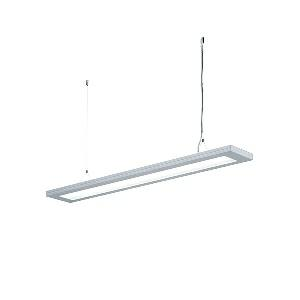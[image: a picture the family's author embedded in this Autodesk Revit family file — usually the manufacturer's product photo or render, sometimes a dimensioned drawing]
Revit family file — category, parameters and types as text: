
# Revit family: lavigo_-_dpp_16000_840_r_g2_00801373_008e
name_source: partatom
category: Lighting Fixtures
units: mm (PartAtom-declared; Revit-internal decimal feet)

## family parameters
Cut with Voids When Loaded = No
Host = Face
Light Source = No
Part Type = Normal
Room Calculation Point = No
Round Connector Dimension = Use Diameter
Shared = No

## types (1)
- LAVIGO - DPP 16000/840/R/G2 (1 x LED, 16450 lm, 4000K)
    Apparent Load = 112 VA
    Approval mark = CE
    CIE Flux Codes = 60 87 97 11 100
    Color Rendering = 80-89
    Color Temperature = 4000K
    Control Gear = Electronic ballast
    Default Elevation = 1800 mm
    Description = DPP 16000/840/R/G2|Suspended luminaire|light source: LED|connected load: 220-240 V, 50/60 Hz|Power consumption: approx. 112 W|standby: approx. 0,50|luminous flux: 16450 lm|luminous efficacy: 146 lm/W|light distribution: Direct/indirect|direct ratio: approx. 11 %|colour temperature: Cold white, ca. 4000 K|color rendering index (CRI): >= 80|chromaticity tolerance:  3 SDCM|System of protection: IP 20|technology: Presence and daylight sensor control (PIR)|luminaire body|material: Steel/plastic|surface: Powder coatet|colour: Silver metallic|lamp cover: Polycarbonate (PC), Clear|mains lead: 1.00 m With free stranded wires|Fastening: Steel cable 0.3 - 0.7 m|decorative contrast side parts: Flint grey|glare control: Prism aperture|luminance(L65): <= 2800 cd/m|unified glare rating(4H 8H): <=  16|special features: Canopy colour (pure white), Push button in luminaire head, Direct light component with edge light and light-guide technology for homogenous light exit, Flicker-free, Integrated light and presence sensor PIR, Retrofittable with TALK module, Separated, direct and indirect light individually adjustable|
    Frequency = 50 Hz
    Height = 36 mm
    Lamp = 1 x LED
    Lamp Light Flux = 16450 lm
    Lamp count = 1
    Length = 1245 mm
    Luminous efficacy = 147 lm/W
    Manufacturer = Waldmann
    ModVariant = No
    Model = 00801373
    Mounting Place = Ceiling
    Mounting Type = Pendant
    Number of Poles = 1
    OnlyDefault = Yes
    Power Factor = 1
    Product Name = LAVIGO - DPP 16000/840/R/G2
    Product group = Suspended luminaire
    ProductGroupID = 9
    Protection Class = Protection class I
    Protection Degree = IP 20
    RLX_Detail_Level = 1
    RLX_Emergency_Light_Flux = 0 lm
    RLX_Emergency_Type = 0
    RLX_Emergency_Type_DB = No
    RlxData = <blob elided: 25377 chars, md5=a239528b>
    Socket = socket
    Standby Power = 0 W
    System Light Flux = 16451 lm
    System Power = 112 W
    Type Comments = Product without accessories
    Type Image = 121740000-00678747.jpg
    URL = http://relux.com
    VarID = ---
    Voltage = 230 V
    Voltage Range = 220-240 V
    Weight = 0.00 kg
    Width = 200 mm  [stored 0.656168 ft]

note: [stored X ft] marks values corroborated as IEEE doubles in the binary element streams (Revit-internal decimal feet)

## geometry (parser evidence)
native form markers: Blend x4, Sweep x14
no freeform markers — native parametric forms only
